# Revit family: LeL Vitre 2.0-2.2
name_source: partatom
category: Lighting Fixtures
units: mm (PartAtom-declared; Revit-internal decimal feet)

## family parameters
Always vertical = No
Cut with Voids When Loaded = No
Light Source = No
OmniClass Number = 23.80.70.00
OmniClass Title = Lighting
Part Type = Normal
Room Calculation Point = No
Round Connector Dimension = Use Diameter
Shared = No
Work Plane-Based = Yes

## types (6) — shared parameters
CCT = 3000 K
CRI = CRI80
Clip in-out = 7 mm  [stored 0.0229659 ft]
Continuous hint = Create a continuous line selecting proper elements
Default Elevation = 1219 mm
Description = Outdoor/underwater linear profiles
IK = IK10
IP = IP65-67
Lamp = LED
Manufacturer = L&L Luce&Light srl
Rated Power supply = 230 V
URL = https://www.lucelight.it

## per-type parameters (varying)
| type | Apparent Load | Connector | End cap | Lenght | Lumen Output | Model | Photometry | Profile lenght | Wattage | Weight |
| 2.0 W 36°x94° 18W | 18 VA | 340 mm | 326 mm  [stored 1.06955 ft] | 644 mm  [stored 2.11286 ft] | 1928 lm | VT20 | VT2 Light source : 2.0 W 36°x94° 18W | 632 mm | 18 W | 1.90 kg |
| 2.0 D 18W | 18 VA | 334 mm | 320 mm  [stored 1.04987 ft] | 632 mm | 2005 lm | VT20 | VT2 Light source : 2.0 D 18W | 620 mm  [stored 2.03412 ft] | 18 W | 1.90 kg |
| 2.1 W 36°x94° 36W | 36 VA | 620 mm  [stored 2.03412 ft] | 606 mm  [stored 1.98819 ft] | 1204 mm  [stored 3.95013 ft] | 3856 lm | VT21 | VT2 Light source : 2.1 W 36°x94° 36W | 1192 mm  [stored 3.91076 ft] | 36 W | 3.00 kg |
| 2.1 D 36W | 36 VA | 620 mm  [stored 2.03412 ft] | 606 mm  [stored 1.98819 ft] | 1204 mm  [stored 3.95013 ft] | 4010 lm | VT21 | VT2 Light source : 2.1 D 36W | 1192 mm  [stored 3.91076 ft] | 36 W | 3.00 kg |
| 2.2 W 36°x94° 58W | 58 VA | 900 mm | 886 mm  [stored 2.90682 ft] | 1764 mm  [stored 5.7874 ft] | 5784 lm | VT22 | VT2 Light source : 2.2 W 36°x94° 58W | 1752 mm  [stored 5.74803 ft] | 58 W | 4.30 kg |
| 2.2 D 58W | 58 VA | 900 mm | 886 mm  [stored 2.90682 ft] | 1764 mm  [stored 5.7874 ft] | 6015 lm | VT22 | VT2 Light source : 2.2 D 58W | 1752 mm  [stored 5.74803 ft] | 58 W | 4.30 kg |

note: [stored X ft] marks values corroborated as IEEE doubles in the binary element streams (Revit-internal decimal feet)

## geometry (parser evidence)
native form markers: Sweep x2
no freeform markers — native parametric forms only
